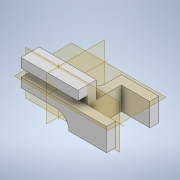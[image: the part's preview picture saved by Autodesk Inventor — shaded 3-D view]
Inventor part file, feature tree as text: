
AUTODESK INVENTOR PART (.ipt)
format: ipt  version: 2022.4 (Build 264492010, 492A)  size: 175,616 bytes
history: native  units: mm
features: extrude x4, sketch x4, mirror x1
ambient origin geometry x8: Origin, YZ Plane, XZ Plane, XY Plane, X Axis, Y Axis, Z Axis, Center Point
bodies: Solid1 (feature_tree)
feature tree (9):
  extrude  "Extrusion1"  Depth=3.0mm
  extrude  "Extrusion2"  Depth=1.6mm
  sketch  "Sketch4"  dims[d3=3.2mm d4=1.6mm]
  sketch  "Sketch5"  dims[d6=4.0mm d7=1.6mm]
  extrude  "Extrusion3"  Depth=1.6mm
  extrude  "Extrusion4"  Depth=10.0mm TaperAngle=0.0deg
  mirror  "Mirror1"
  sketch  "Sketch3"  dims[d1=6.0mm d2=3.0mm]
  sketch  "Sketch6"  dims[d8=1.4mm d10=10.0mm d11=0.0mm d12=1.6mm d14=1.6mm d15=1.6mm d17=2.4mm d18=0.0mm d19=0.0mm d20=1.6mm d21=1.6mm d22=5.0mm d23=0.0mm d24=1.6mm d25=1.6mm d26=1.6mm d27=0.0mm d28=0.0mm]
